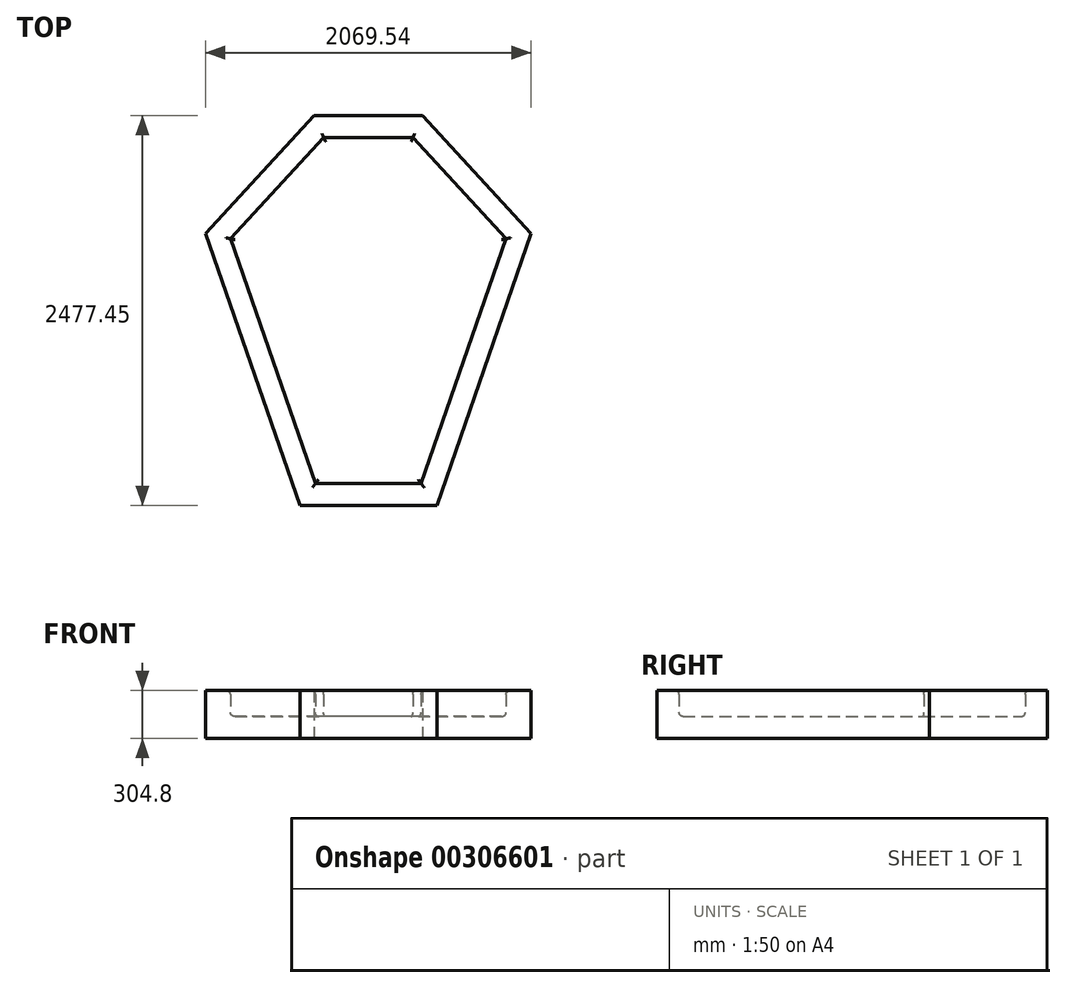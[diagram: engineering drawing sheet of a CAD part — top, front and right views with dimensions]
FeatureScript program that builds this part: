
annotation { "Feature Type Name" : "Feature", "Feature Type Description" : "" }
export const myFeature = defineFeature(function(context is Context, id is Id, definition is map)
    precondition{}
    {
        {
            var Q0;
            Q0=qCreatedBy(makeId("Top.planeOp"),FACE);
            var sketch = newSketch(context, id + "F0", { "sketchPlane" : qUnion([Q0])});
            skLineSegment(sketch, "E0", {"start": v(0, -1163.74) * mm, "end": v(-434.9, -1163.74) * mm});
            skLineSegment(sketch, "E1", {"start": v(-434.9, -1163.74) * mm, "end": v(-1034.77, 563.88) * mm});
            skLineSegment(sketch, "E2", {"start": v(-1034.77, 563.88) * mm, "end": v(-344.92, 1313.71) * mm});
            skLineSegment(sketch, "E3", {"start": v(-344.92, 1313.71) * mm, "end": v(0, 1313.71) * mm});
            skLineSegment(sketch, "E4.MirrorCS", {"start": v(344.92, 1313.71) * mm, "end": v(0, 1313.71) * mm});
            skLineSegment(sketch, "E5.MirrorCS", {"start": v(1034.77, 563.88) * mm, "end": v(344.92, 1313.71) * mm});
            skLineSegment(sketch, "E6.MirrorCS", {"start": v(434.9, -1163.74) * mm, "end": v(1034.77, 563.88) * mm});
            skLineSegment(sketch, "E7.MirrorCS", {"start": v(0, -1163.74) * mm, "end": v(434.9, -1163.74) * mm});
            skSolve(sketch);
        }
        {
            var Q0;
            Q0 = qSketchRegion(id + "F0", true);
            extrude(context, id + "F1", {"entities" : qUnion([Q0]), "depth" : 304.8 * mm});
        }
        {
            var Q0;
            Q0=makeQuery(id+"F1.opExtrude","CAP_FACE",FACE,{"disambiguationData":[OSD([sQuery(id+"F0.wireOp",EDGE,"E0"),sQuery(id+"F0.wireOp",EDGE,"E1"),sQuery(id+"F0.wireOp",EDGE,"E2"),sQuery(id+"F0.wireOp",EDGE,"E3"),sQuery(id+"F0.wireOp",EDGE,"E4.MirrorCS"),sQuery(id+"F0.wireOp",EDGE,"E5.MirrorCS"),sQuery(id+"F0.wireOp",EDGE,"E6.MirrorCS"),sQuery(id+"F0.wireOp",EDGE,"E7.MirrorCS")])],"isStart":false});
            shell(context, id + "F2", {"entities" : qUnion([Q0]), "thickness" : 139.7 * mm});
        }
        {
            var Q0;
            {var subQ0=sQuery(id+"F0.wireOp",EDGE,"E2");Q0=makeQuery(id+"F2.opShell","OFFSET_EDGE",EDGE,{"disambiguationData":[OSD([subQ0]),TDD([makeQuery(id+"F1.opExtrude","CAP_EDGE",EDGE,{"disambiguationData":[OSD([subQ0])],"isStart":false})])]});}
            var Q1;
            {var subQ0=sQuery(id+"F0.wireOp",EDGE,"E4.MirrorCS");var subQ1=sQuery(id+"F0.wireOp",EDGE,"E3");Q1=makeQuery(id+"F2.opShell","OFFSET_EDGE",EDGE,{"disambiguationData":[OSD([subQ1,subQ0]),TDD([makeQuery(id+"F1.opExtrude","CAP_EDGE",EDGE,{"disambiguationData":[OSD([subQ1,subQ0])],"isStart":false})])]});}
            var Q2;
            {var subQ0=sQuery(id+"F0.wireOp",EDGE,"E5.MirrorCS");Q2=makeQuery(id+"F2.opShell","OFFSET_EDGE",EDGE,{"disambiguationData":[OSD([subQ0]),TDD([makeQuery(id+"F1.opExtrude","CAP_EDGE",EDGE,{"disambiguationData":[OSD([subQ0])],"isStart":false})])]});}
            var Q3;
            {var subQ0=sQuery(id+"F0.wireOp",EDGE,"E6.MirrorCS");Q3=makeQuery(id+"F2.opShell","OFFSET_EDGE",EDGE,{"disambiguationData":[OSD([subQ0]),TDD([makeQuery(id+"F1.opExtrude","CAP_EDGE",EDGE,{"disambiguationData":[OSD([subQ0])],"isStart":false})])]});}
            var Q4;
            {var subQ0=sQuery(id+"F0.wireOp",EDGE,"E7.MirrorCS");var subQ1=sQuery(id+"F0.wireOp",EDGE,"E0");Q4=makeQuery(id+"F2.opShell","OFFSET_EDGE",EDGE,{"disambiguationData":[OSD([subQ1,subQ0]),TDD([makeQuery(id+"F1.opExtrude","CAP_EDGE",EDGE,{"disambiguationData":[OSD([subQ1,subQ0])],"isStart":false})])]});}
            var Q5;
            {var subQ0=sQuery(id+"F0.wireOp",EDGE,"E1");Q5=makeQuery(id+"F2.opShell","OFFSET_EDGE",EDGE,{"disambiguationData":[OSD([subQ0]),TDD([makeQuery(id+"F1.opExtrude","CAP_EDGE",EDGE,{"disambiguationData":[OSD([subQ0])],"isStart":false})])]});}
            fillet(context, id + "F3", {"entities" : qUnion([Q0, Q1, Q2, Q3, Q4, Q5]), "radius" : 25.4 * mm, "tangentPropagation" : true, "allowEdgeOverflow" : false});
        }
        {
            var Q0;
            Q0=makeQuery(id+"F2.opShell","OFFSET_FACE",FACE,{"disambiguationData":[OSD([sQuery(id+"F0.wireOp",EDGE,"E0"),sQuery(id+"F0.wireOp",EDGE,"E1"),sQuery(id+"F0.wireOp",EDGE,"E2"),sQuery(id+"F0.wireOp",EDGE,"E3"),sQuery(id+"F0.wireOp",EDGE,"E4.MirrorCS"),sQuery(id+"F0.wireOp",EDGE,"E5.MirrorCS"),sQuery(id+"F0.wireOp",EDGE,"E6.MirrorCS"),sQuery(id+"F0.wireOp",EDGE,"E7.MirrorCS")])]});
            fillet(context, id + "F4", {"entities" : qUnion([Q0]), "radius" : 25.4 * mm, "tangentPropagation" : true, "allowEdgeOverflow" : false});
        }
    });
